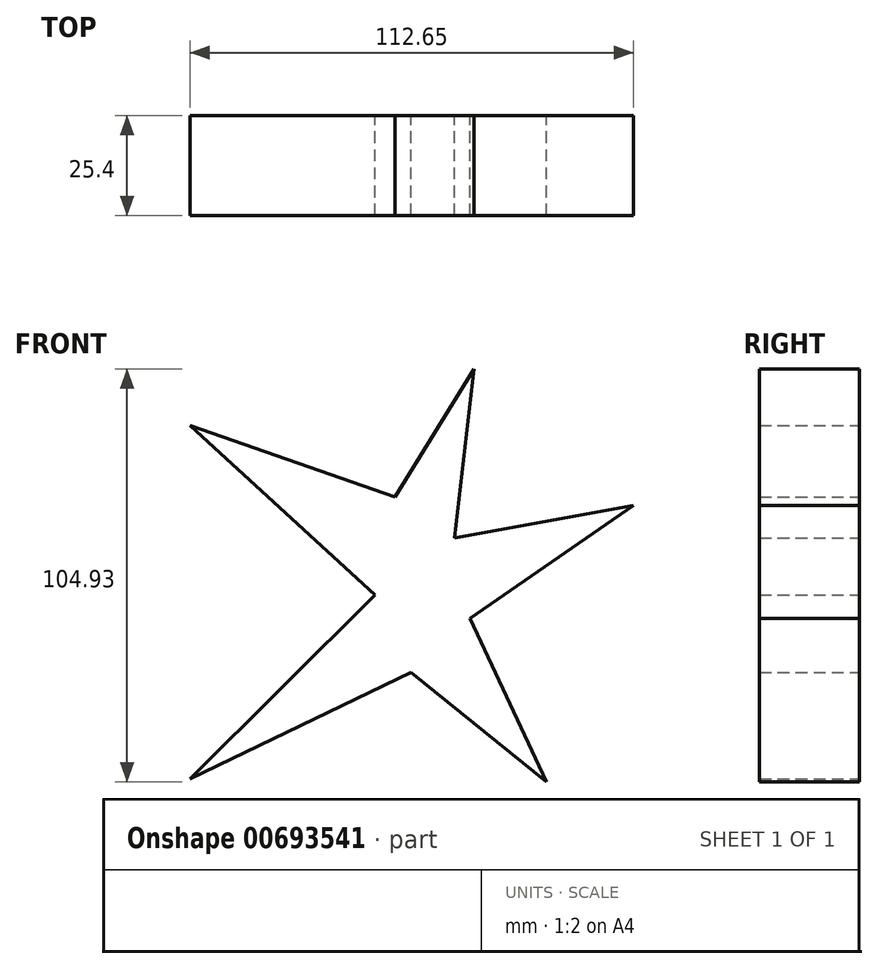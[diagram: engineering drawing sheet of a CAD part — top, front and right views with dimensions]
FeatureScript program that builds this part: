
annotation { "Feature Type Name" : "Feature", "Feature Type Description" : "" }
export const myFeature = defineFeature(function(context is Context, id is Id, definition is map)
    precondition{}
    {
        {
            var Q0;
            Q0=qCreatedBy(makeId("Front.planeOp"),FACE);
            var sketch = newSketch(context, id + "F0", { "sketchPlane" : qUnion([Q0])});
            skLineSegment(sketch, "E0", {"start": v(0, 0) * mm, "end": v(-46.96, 43.1) * mm});
            skLineSegment(sketch, "E1", {"start": v(-46.96, 43.1) * mm, "end": v(5.1, 24.93) * mm});
            skLineSegment(sketch, "E2", {"start": v(5.1, 24.93) * mm, "end": v(25.2, 57.42) * mm});
            skLineSegment(sketch, "E3", {"start": v(25.2, 57.42) * mm, "end": v(20.24, 14.46) * mm});
            skLineSegment(sketch, "E4", {"start": v(20.24, 14.46) * mm, "end": v(65.69, 22.72) * mm});
            skLineSegment(sketch, "E5", {"start": v(65.69, 22.72) * mm, "end": v(24.1, -5.92) * mm});
            skLineSegment(sketch, "E6", {"start": v(24.1, -5.92) * mm, "end": v(43.65, -47.5) * mm});
            skLineSegment(sketch, "E7", {"start": v(43.65, -47.5) * mm, "end": v(9.23, -19.7) * mm});
            skLineSegment(sketch, "E8", {"start": v(9.23, -19.7) * mm, "end": v(-46.96, -46.68) * mm});
            skLineSegment(sketch, "E9", {"start": v(-46.96, -46.68) * mm, "end": v(0, 0) * mm});
            skSolve(sketch);
        }
        {
            var Q0;
            Q0 = qSketchRegion(id + "F0", true);
            extrude(context, id + "F1", {"entities" : qUnion([Q0]), "depth" : 25.4 * mm, "offsetDistance" : 25.4 * mm});
        }
    });
